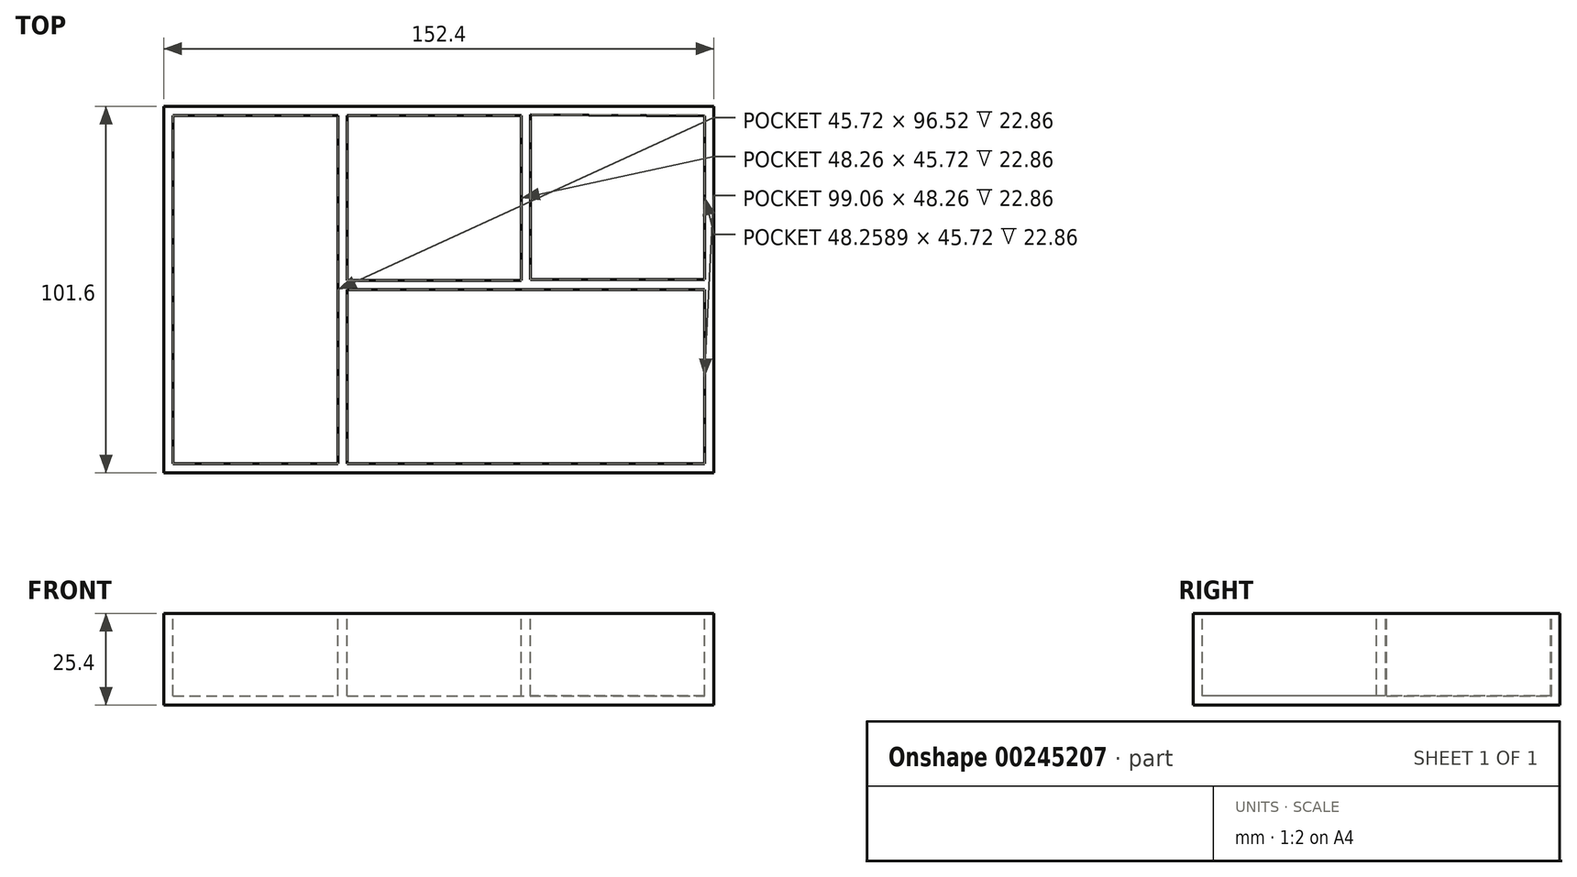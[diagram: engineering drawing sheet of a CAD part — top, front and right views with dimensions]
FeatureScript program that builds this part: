
annotation { "Feature Type Name" : "Feature", "Feature Type Description" : "" }
export const myFeature = defineFeature(function(context is Context, id is Id, definition is map)
    precondition{}
    {
        {
            var Q0;
            Q0=qCreatedBy(makeId("Top.planeOp"),FACE);
            var sketch = newSketch(context, id + "F0", { "sketchPlane" : qUnion([Q0])});
            skLineSegment(sketch, "E0.bottom", {"start": v(0, 0) * mm, "end": v(152.4, 0) * mm});
            skLineSegment(sketch, "E0.top", {"start": v(0, 101.6) * mm, "end": v(152.4, 101.6) * mm});
            skLineSegment(sketch, "E0.left", {"start": v(0, 0) * mm, "end": v(0, 101.6) * mm});
            skLineSegment(sketch, "E0.right", {"start": v(152.4, 0) * mm, "end": v(152.4, 101.6) * mm});
            skSolve(sketch);
        }
        {
            var Q0;
            Q0=makeQuery(id+"F0.imprint","IMPRINT",FACE,{"disambiguationData":[TD([[makeQuery(id+"F0.imprint","IMPRINT",EDGE,{"derivedFrom":sQuery(id+"F0.wireOp",EDGE,"E0.bottom")}),1.0]])]});
            extrude(context, id + "F1", {"entities" : qUnion([Q0]), "depth" : 25.4 * mm});
        }
        {
            var Q0;
            Q0=makeQuery(id+"F1.opExtrude","CAP_FACE",FACE,{"disambiguationData":[OSD([sQuery(id+"F0.wireOp",EDGE,"E0.bottom"),sQuery(id+"F0.wireOp",EDGE,"E0.top"),sQuery(id+"F0.wireOp",EDGE,"E0.left"),sQuery(id+"F0.wireOp",EDGE,"E0.right")])],"isStart":false});
            var sketch = newSketch(context, id + "F2", { "sketchPlane" : qUnion([Q0])});
            skLineSegment(sketch, "E1.bottom", {"start": v(2.54, 99.06) * mm, "end": v(48.26, 99.06) * mm});
            skLineSegment(sketch, "E1.top", {"start": v(2.54, 2.54) * mm, "end": v(48.26, 2.54) * mm});
            skLineSegment(sketch, "E1.left", {"start": v(2.54, 99.06) * mm, "end": v(2.54, 2.54) * mm});
            skLineSegment(sketch, "E1.right", {"start": v(48.26, 99.06) * mm, "end": v(48.26, 2.54) * mm});
            skLineSegment(sketch, "E2", {"start": v(2.54, 62.21) * mm, "end": v(0, 62.21) * mm});
            skLineSegment(sketch, "E3", {"start": v(22.02, 99.06) * mm, "end": v(22.02, 101.6) * mm});
            skSolve(sketch);
        }
        {
            var Q0;
            {var subQ4=sQuery(id+"F2.wireOp",EDGE,"E1.top");Q0=makeQuery(id+"F2.imprint","IMPRINT",FACE,{"disambiguationData":[TD([[makeQuery(id+"F2.imprint","IMPRINT",EDGE,{"derivedFrom":subQ4}),1.0]])]});}
            extrude(context, id + "F3", {"entities" : qUnion([Q0]), "operationType" : NewBodyOperationType.REMOVE, "oppositeDirection" : true, "depth" : 22.86 * mm});
        }
        {
            var Q0;
            Q0=makeQuery(id+"F1.opExtrude","CAP_FACE",FACE,{"disambiguationData":[OSD([sQuery(id+"F0.wireOp",EDGE,"E0.bottom"),sQuery(id+"F0.wireOp",EDGE,"E0.top"),sQuery(id+"F0.wireOp",EDGE,"E0.left"),sQuery(id+"F0.wireOp",EDGE,"E0.right")])],"isStart":false});
            var sketch = newSketch(context, id + "F4", { "sketchPlane" : qUnion([Q0])});
            skLineSegment(sketch, "E4.bottom", {"start": v(50.8, 99.06) * mm, "end": v(99.06, 99.06) * mm});
            skLineSegment(sketch, "E4.top", {"start": v(50.8, 53.34) * mm, "end": v(99.06, 53.34) * mm});
            skLineSegment(sketch, "E4.left", {"start": v(50.8, 99.06) * mm, "end": v(50.8, 53.34) * mm});
            skLineSegment(sketch, "E4.right", {"start": v(99.06, 99.06) * mm, "end": v(99.06, 53.34) * mm});
            skLineSegment(sketch, "E5", {"start": v(50.8, 76.2) * mm, "end": v(48.26, 76.2) * mm});
            skLineSegment(sketch, "E6", {"start": v(67.74, 99.06) * mm, "end": v(67.74, 101.6) * mm});
            skSolve(sketch);
        }
        {
            var Q0;
            {var subQ6=sQuery(id+"F4.wireOp",EDGE,"E4.top");Q0=makeQuery(id+"F4.imprint","IMPRINT",FACE,{"disambiguationData":[TD([[makeQuery(id+"F4.imprint","IMPRINT",EDGE,{"derivedFrom":subQ6}),1.0]])]});}
            extrude(context, id + "F5", {"entities" : qUnion([Q0]), "operationType" : NewBodyOperationType.REMOVE, "oppositeDirection" : true, "depth" : 22.86 * mm});
        }
        {
            var Q0;
            Q0=makeQuery(id+"F1.opExtrude","CAP_FACE",FACE,{"disambiguationData":[OSD([sQuery(id+"F0.wireOp",EDGE,"E0.bottom"),sQuery(id+"F0.wireOp",EDGE,"E0.top"),sQuery(id+"F0.wireOp",EDGE,"E0.left"),sQuery(id+"F0.wireOp",EDGE,"E0.right")])],"isStart":false});
            var sketch = newSketch(context, id + "F6", { "sketchPlane" : qUnion([Q0])});
            skLineSegment(sketch, "E7.bottom", {"start": v(50.8, 50.8) * mm, "end": v(149.86, 50.8) * mm});
            skLineSegment(sketch, "E7.top", {"start": v(50.8, 2.54) * mm, "end": v(149.86, 2.54) * mm});
            skLineSegment(sketch, "E7.left", {"start": v(50.8, 50.8) * mm, "end": v(50.8, 2.54) * mm});
            skLineSegment(sketch, "E7.right", {"start": v(149.86, 50.8) * mm, "end": v(149.86, 2.54) * mm});
            skLineSegment(sketch, "E8", {"start": v(50.8, 26.67) * mm, "end": v(48.26, 26.67) * mm});
            skLineSegment(sketch, "E9", {"start": v(74.93, 53.34) * mm, "end": v(74.93, 50.8) * mm});
            skSolve(sketch);
        }
        {
            var Q0;
            {var subQ4=sQuery(id+"F6.wireOp",EDGE,"E7.top");Q0=makeQuery(id+"F6.imprint","IMPRINT",FACE,{"disambiguationData":[TD([[makeQuery(id+"F6.imprint","IMPRINT",EDGE,{"derivedFrom":subQ4}),1.0]])]});}
            extrude(context, id + "F7", {"entities" : qUnion([Q0]), "operationType" : NewBodyOperationType.REMOVE, "oppositeDirection" : true, "depth" : 22.86 * mm});
        }
        {
            var Q0;
            Q0=makeQuery(id+"F1.opExtrude","CAP_FACE",FACE,{"disambiguationData":[OSD([sQuery(id+"F0.wireOp",EDGE,"E0.bottom"),sQuery(id+"F0.wireOp",EDGE,"E0.top"),sQuery(id+"F0.wireOp",EDGE,"E0.left"),sQuery(id+"F0.wireOp",EDGE,"E0.right")])],"isStart":false});
            var sketch = newSketch(context, id + "F8", { "sketchPlane" : qUnion([Q0])});
            skLineSegment(sketch, "E10", {"start": v(101.6, 99.31) * mm, "end": v(101.6, 53.6) * mm});
            skLineSegment(sketch, "E11", {"start": v(101.6, 53.6) * mm, "end": v(149.86, 53.6) * mm});
            skLineSegment(sketch, "E12", {"start": v(149.86, 53.6) * mm, "end": v(149.86, 99) * mm});
            skLineSegment(sketch, "E13", {"start": v(149.86, 99) * mm, "end": v(101.6, 99.31) * mm});
            skSolve(sketch);
        }
        {
            var Q0;
            Q0=makeQuery(id+"F8.imprint","IMPRINT",FACE,{"disambiguationData":[TD([[makeQuery(id+"F8.imprint","IMPRINT",EDGE,{"derivedFrom":sQuery(id+"F8.wireOp",EDGE,"E10")}),1.0]])]});
            extrude(context, id + "F9", {"entities" : qUnion([Q0]), "operationType" : NewBodyOperationType.REMOVE, "oppositeDirection" : true, "depth" : 22.86 * mm});
        }
    });
